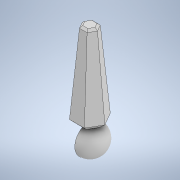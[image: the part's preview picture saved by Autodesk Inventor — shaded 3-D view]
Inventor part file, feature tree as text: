
AUTODESK INVENTOR PART (.ipt)
format: ipt  version: 2022 (Build 260153000, 153)  size: 153,088 bytes
history: native  units: in
note: dims shown in document units (in); Inventor stores cm internally (conversion verified against a paired STEP export)
features: sketch x5, revolve x2, sweep x1, hole x1
ambient origin geometry x8: Origin, YZ Plane, XZ Plane, XY Plane, X Axis, Y Axis, Z Axis, Center Point
bodies: Solid1 (feature_tree)
feature tree (9):
  sweep  "Sweep1"
  revolve  "Revolution2"  [1 undecoded]
  revolve  "Revolution3"  [1 undecoded]
  hole  "Hole1"  [1 undecoded]
  sketch  "Sketch1"  dims[d3=0.0in d4=0.0in d6=180.0deg]
  sketch  "Sketch2"  dims[d7=180.0deg]
  sketch  "Sketch3"  dims[d8=0.03in d9=0.75in d10=0.119in d11=0.25in d12=0.5635in d13=0.06in d14=0.8108in d2=0.0344in]
  sketch  "Sketch4"  dims[d5=0.0344in]
  sketch  "Sketch5"
note: 3 required parameter values undecoded (feature->parameter linkage not recoverable at this tier; creation-order binding heuristic only, values carry confidence <= 0.55)